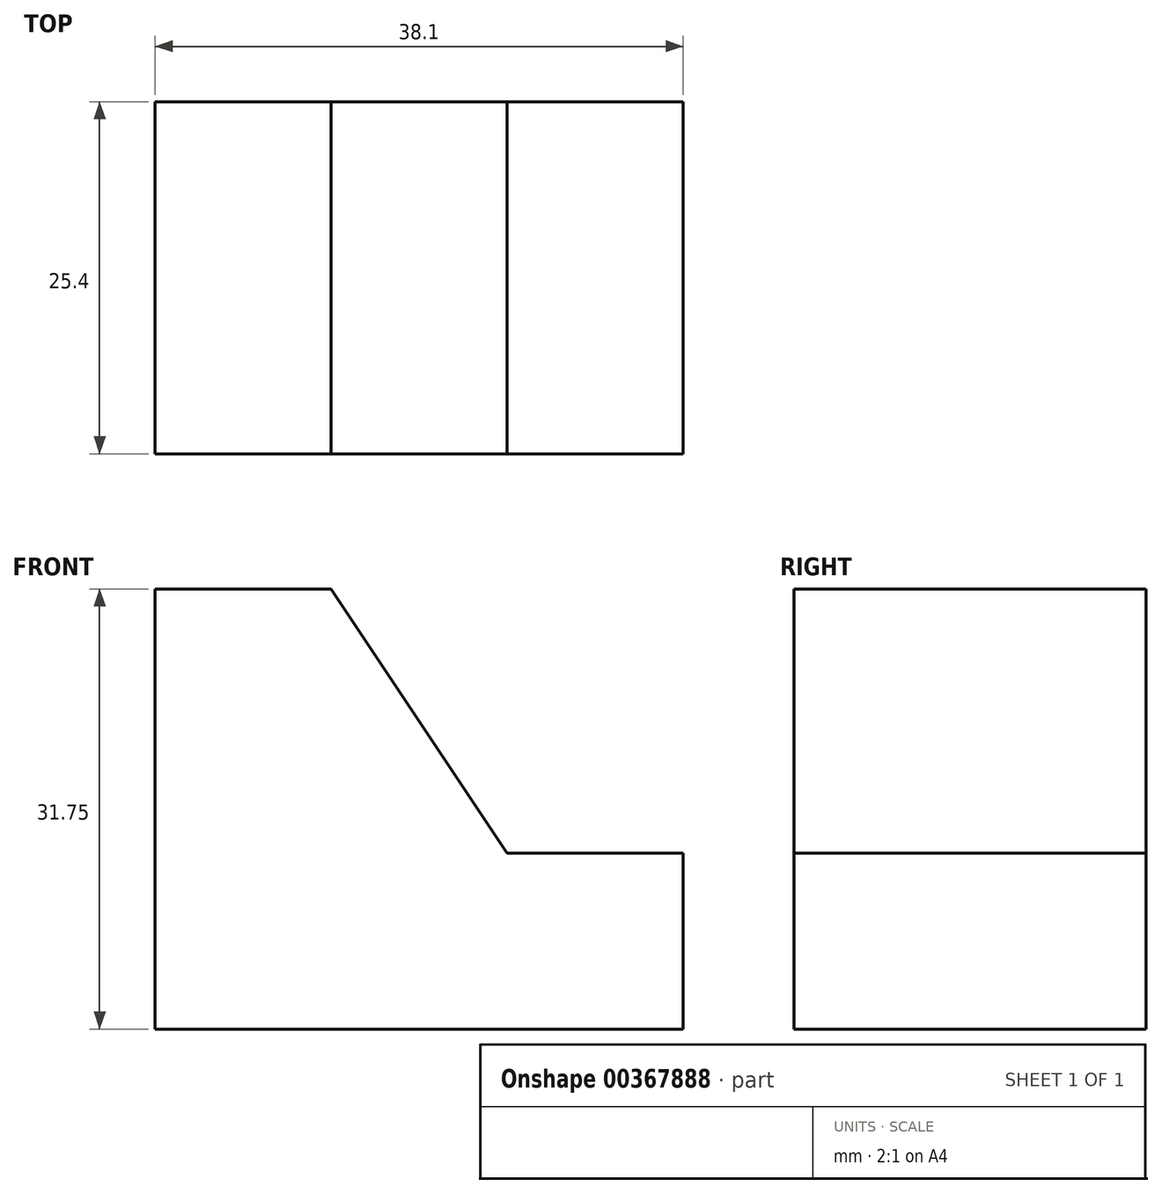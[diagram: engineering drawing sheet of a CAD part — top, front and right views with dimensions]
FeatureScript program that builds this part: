
annotation { "Feature Type Name" : "Feature", "Feature Type Description" : "" }
export const myFeature = defineFeature(function(context is Context, id is Id, definition is map)
    precondition{}
    {
        {
            var Q0;
            Q0=qCreatedBy(makeId("Front.planeOp"),FACE);
            var sketch = newSketch(context, id + "F0", { "sketchPlane" : qUnion([Q0])});
            skLineSegment(sketch, "E0", {"start": v(-30.52, 31.75) * mm, "end": v(-30.52, 0) * mm});
            skLineSegment(sketch, "E1", {"start": v(-30.52, 31.75) * mm, "end": v(-17.82, 31.75) * mm});
            skLineSegment(sketch, "E2", {"start": v(-30.52, 0) * mm, "end": v(7.58, 0) * mm});
            skLineSegment(sketch, "E3", {"start": v(7.58, 0) * mm, "end": v(7.58, 12.7) * mm});
            skLineSegment(sketch, "E4", {"start": v(7.58, 12.7) * mm, "end": v(-5.12, 12.7) * mm});
            skLineSegment(sketch, "E5", {"start": v(-17.82, 31.75) * mm, "end": v(-5.12, 12.7) * mm});
            skSolve(sketch);
        }
        {
            var Q0;
            Q0=makeQuery(id+"F0.imprint","IMPRINT",FACE,{"disambiguationData":[TD([[makeQuery(id+"F0.imprint","IMPRINT",EDGE,{"derivedFrom":sQuery(id+"F0.wireOp",EDGE,"E0")}),1.0]])]});
            extrude(context, id + "F1", {"entities" : qUnion([Q0]), "depth" : 25.4 * mm});
        }
    });
